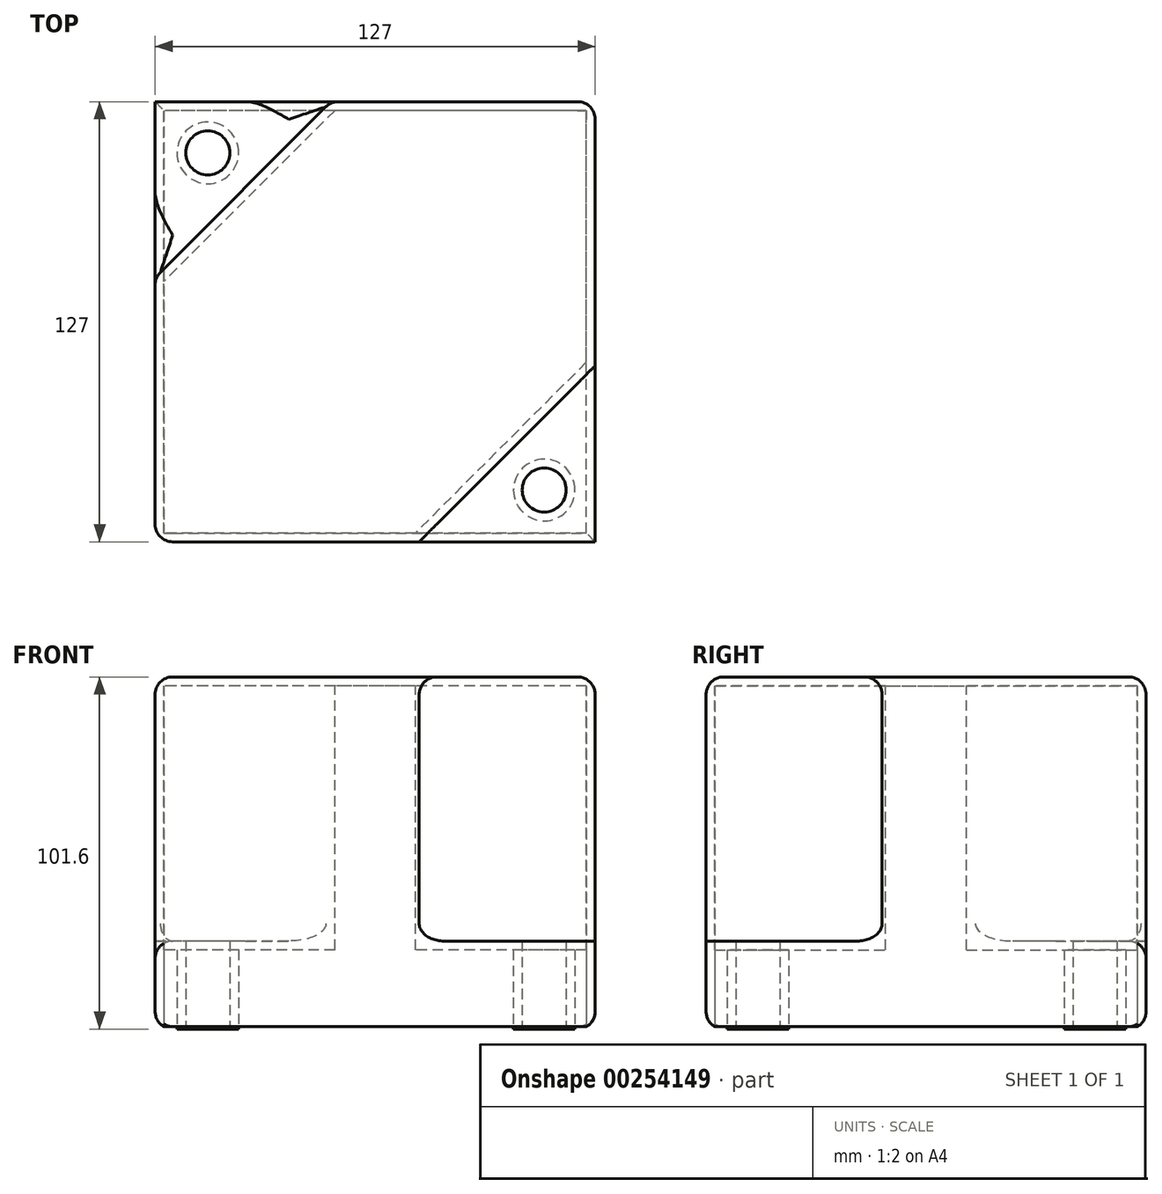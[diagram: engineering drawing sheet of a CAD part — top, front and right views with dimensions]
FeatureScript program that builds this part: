
annotation { "Feature Type Name" : "Feature", "Feature Type Description" : "" }
export const myFeature = defineFeature(function(context is Context, id is Id, definition is map)
    precondition{}
    {
        {
            var Q0;
            Q0=qCreatedBy(makeId("Top.planeOp"),FACE);
            var sketch = newSketch(context, id + "F0", { "sketchPlane" : qUnion([Q0])});
            skLineSegment(sketch, "E0.bottom", {"start": v(63.5, -63.5) * mm, "end": v(-63.5, -63.5) * mm});
            skLineSegment(sketch, "E0.top", {"start": v(63.5, 63.5) * mm, "end": v(-63.5, 63.5) * mm});
            skLineSegment(sketch, "E0.left", {"start": v(63.5, -63.5) * mm, "end": v(63.5, 63.5) * mm});
            skLineSegment(sketch, "E0.right", {"start": v(-63.5, -63.5) * mm, "end": v(-63.5, 63.5) * mm});
            skPoint(sketch, "E0.middle", {"position": v(0, 0) * mm});
            skSolve(sketch);
        }
        {
            var Q0;
            Q0=makeQuery(id+"F0.imprint","IMPRINT",FACE,{"disambiguationData":[TD([[makeQuery(id+"F0.imprint","IMPRINT",EDGE,{"derivedFrom":sQuery(id+"F0.wireOp",EDGE,"E0.bottom")}),-1.0]])]});
            extrude(context, id + "F1", {"entities" : qUnion([Q0]), "depth" : 101.6 * mm});
        }
        {
            var Q0;
            Q0=makeQuery(id+"F1.opExtrude","CAP_FACE",FACE,{"disambiguationData":[OSD([sQuery(id+"F0.wireOp",EDGE,"E0.bottom"),sQuery(id+"F0.wireOp",EDGE,"E0.top"),sQuery(id+"F0.wireOp",EDGE,"E0.left"),sQuery(id+"F0.wireOp",EDGE,"E0.right")])],"isStart":false});
            var sketch = newSketch(context, id + "F2", { "sketchPlane" : qUnion([Q0])});
            skLineSegment(sketch, "E1", {"start": v(-12.7, 63.5) * mm, "end": v(-63.5, 12.7) * mm});
            skLineSegment(sketch, "E2", {"start": v(63.5, -12.7) * mm, "end": v(12.7, -63.5) * mm});
            skSolve(sketch);
        }
        {
            var Q0;
            {var subQ0=sQuery(id+"F2.wireOp",EDGE,"E1");Q0=makeQuery(id+"F2.imprint","IMPRINT",FACE,{"disambiguationData":[TD([[makeQuery(id+"F2.imprint","IMPRINT",EDGE,{"derivedFrom":subQ0}),-1.0]])]});}
            var Q1;
            {var subQ0=sQuery(id+"F2.wireOp",EDGE,"E2");Q1=makeQuery(id+"F2.imprint","IMPRINT",FACE,{"disambiguationData":[TD([[makeQuery(id+"F2.imprint","IMPRINT",EDGE,{"derivedFrom":subQ0}),1.0]])]});}
            extrude(context, id + "F3", {"entities" : qUnion([Q0, Q1]), "operationType" : NewBodyOperationType.REMOVE, "oppositeDirection" : true, "depth" : 76.2 * mm});
        }
        {
            var Q0;
            Q0=qCreatedBy(makeId("Top.planeOp"),FACE);
            var sketch = newSketch(context, id + "F4", { "sketchPlane" : qUnion([Q0])});
            skCircle(sketch, "E3", {"center": v(48.8, -48.57) * mm, "radius": 6.35 * mm});
            skLineSegment(sketch, "E4", {"start": v(48.8, -48.57) * mm, "end": v(64.03, -48.57) * mm});
            skLineSegment(sketch, "E5", {"start": v(48.8, -48.57) * mm, "end": v(48.8, -63.81) * mm});
            skLineSegment(sketch, "E6", {"start": v(-63.54, 63.95) * mm, "end": v(-48.3, 63.95) * mm});
            skLineSegment(sketch, "E7", {"start": v(-63.54, 63.95) * mm, "end": v(-63.54, 48.71) * mm});
            skLineSegment(sketch, "E8", {"start": v(-48.3, 63.95) * mm, "end": v(-48.3, 48.71) * mm});
            skCircle(sketch, "E9", {"center": v(-48.3, 48.71) * mm, "radius": 6.35 * mm});
            skSolve(sketch);
        }
        {
            var Q0;
            Q0=makeQuery(id+"F4.imprint","IMPRINT",FACE,{"disambiguationData":[TD([[makeQuery(id+"F4.imprint","IMPRINT",EDGE,{"derivedFrom":sQuery(id+"F4.wireOp",EDGE,"E9")}),1.0]])]});
            var Q1;
            {var subQ0=sQuery(id+"F4.wireOp",EDGE,"E4");var subQ1=sQuery(id+"F4.wireOp",EDGE,"E3");var subQ2=makeQuery(id+"F4.imprint","INTERSECT",VERTEX,{"derivedFrom":[subQ1,subQ0]});Q1=makeQuery(id+"F4.imprint","IMPRINT",FACE,{"disambiguationData":[TD([[makeQuery(id+"F4.imprint","IMPRINT",EDGE,{"disambiguationData":[TD([[subQ2,-1.0]])],"derivedFrom":subQ1}),1.0]])]});}
            var Q2;
            {var subQ0=sQuery(id+"F4.wireOp",EDGE,"E4");var subQ1=sQuery(id+"F4.wireOp",EDGE,"E3");var subQ2=makeQuery(id+"F4.imprint","INTERSECT",VERTEX,{"derivedFrom":[subQ1,subQ0]});Q2=makeQuery(id+"F4.imprint","IMPRINT",FACE,{"disambiguationData":[TD([[makeQuery(id+"F4.imprint","IMPRINT",EDGE,{"disambiguationData":[TD([[subQ2,1.0]])],"derivedFrom":subQ1}),1.0]])]});}
            var Q3;
            Q3=makeQuery(id+"F3.boolean.opBoolean","COPY",FACE,{"derivedFrom":makeQuery(id+"F3.opExtrude","CAP_FACE",FACE,{"disambiguationData":[OSD([sQuery(id+"F0.wireOp",EDGE,"E0.bottom"),sQuery(id+"F0.wireOp",EDGE,"E0.left"),sQuery(id+"F2.wireOp",EDGE,"E2")])],"isStart":false})});
            extrude(context, id + "F5", {"entities" : qUnion([Q0, Q1, Q2]), "operationType" : NewBodyOperationType.REMOVE, "endBound" : BoundingType.UP_TO_SURFACE, "endBoundEntityFace" : qUnion([Q3]), "depth" : 203.2 * mm});
        }
        {
            var Q0;
            Q0=makeQuery(id+"F1.opExtrude","CAP_FACE",FACE,{"disambiguationData":[OSD([sQuery(id+"F0.wireOp",EDGE,"E0.bottom"),sQuery(id+"F0.wireOp",EDGE,"E0.top"),sQuery(id+"F0.wireOp",EDGE,"E0.left"),sQuery(id+"F0.wireOp",EDGE,"E0.right")])],"isStart":true});
            shell(context, id + "F6", {"entities" : qUnion([Q0]), "thickness" : 2.54 * mm});
        }
        {
            var Q0;
            Q0=makeQuery(id+"F3.boolean.opBoolean","COPY",EDGE,{"derivedFrom":makeQuery(id+"F3.opExtrude","CAP_EDGE",EDGE,{"disambiguationData":[OSD([sQuery(id+"F2.wireOp",EDGE,"E2")])],"isStart":true})});
            var Q1;
            Q1=makeQuery(id+"F1.opExtrude","CAP_EDGE",EDGE,{"disambiguationData":[OSD([sQuery(id+"F0.wireOp",EDGE,"E0.bottom")])],"isStart":false});
            var Q2;
            Q2=makeQuery(id+"F1.opExtrude","CAP_EDGE",EDGE,{"disambiguationData":[OSD([sQuery(id+"F0.wireOp",EDGE,"E0.left")])],"isStart":false});
            var Q3;
            Q3=makeQuery(id+"F1.opExtrude","CAP_EDGE",EDGE,{"disambiguationData":[OSD([sQuery(id+"F0.wireOp",EDGE,"E0.right")])],"isStart":false});
            var Q4;
            Q4=makeQuery(id+"F3.boolean.opBoolean","COPY",EDGE,{"derivedFrom":makeQuery(id+"F3.opExtrude","CAP_EDGE",EDGE,{"disambiguationData":[OSD([sQuery(id+"F2.wireOp",EDGE,"E1")])],"isStart":true})});
            var Q5;
            Q5=makeQuery(id+"F1.opExtrude","CAP_EDGE",EDGE,{"disambiguationData":[OSD([sQuery(id+"F0.wireOp",EDGE,"E0.top")])],"isStart":false});
            var Q6;
            Q6=makeQuery(id+"F3.boolean.opBoolean","COPY",EDGE,{"derivedFrom":makeQuery(id+"F3.opExtrude","CAP_EDGE",EDGE,{"disambiguationData":[OSD([sQuery(id+"F0.wireOp",EDGE,"E0.top")])],"isStart":false})});
            var Q7;
            Q7=makeQuery(id+"F3.boolean.opBoolean","COPY",EDGE,{"derivedFrom":makeQuery(id+"F3.opExtrude","SWEPT_EDGE",EDGE,{"disambiguationData":[OSD([sQuery(id+"F0.wireOp",EDGE,"E0.top"),sQuery(id+"F2.wireOp",EDGE,"E1")])]})});
            var Q8;
            Q8=makeQuery(id+"F3.boolean.opBoolean","COPY",FACE,{"derivedFrom":makeQuery(id+"F3.opExtrude","SWEPT_FACE",FACE,{"disambiguationData":[OSD([sQuery(id+"F2.wireOp",EDGE,"E1")])]})});
            var Q9;
            Q9=makeQuery(id+"F3.boolean.opBoolean","COPY",EDGE,{"derivedFrom":makeQuery(id+"F3.opExtrude","SWEPT_EDGE",EDGE,{"disambiguationData":[OSD([sQuery(id+"F0.wireOp",EDGE,"E0.bottom"),sQuery(id+"F2.wireOp",EDGE,"E2")])]})});
            var Q10;
            Q10=makeQuery(id+"F3.boolean.opBoolean","COPY",EDGE,{"derivedFrom":makeQuery(id+"F3.opExtrude","SWEPT_EDGE",EDGE,{"disambiguationData":[OSD([sQuery(id+"F0.wireOp",EDGE,"E0.left"),sQuery(id+"F2.wireOp",EDGE,"E2")])]})});
            var Q11;
            Q11=makeQuery(id+"F3.boolean.opBoolean","COPY",EDGE,{"derivedFrom":makeQuery(id+"F3.opExtrude","CAP_EDGE",EDGE,{"disambiguationData":[OSD([sQuery(id+"F0.wireOp",EDGE,"E0.left")])],"isStart":false})});
            var Q12;
            Q12=makeQuery(id+"F3.boolean.opBoolean","COPY",EDGE,{"derivedFrom":makeQuery(id+"F3.opExtrude","CAP_EDGE",EDGE,{"disambiguationData":[OSD([sQuery(id+"F0.wireOp",EDGE,"E0.bottom")])],"isStart":false})});
            var Q13;
            Q13=makeQuery(id+"F1.opExtrude","CAP_EDGE",EDGE,{"disambiguationData":[OSD([sQuery(id+"F0.wireOp",EDGE,"E0.left")])],"isStart":true});
            var Q14;
            Q14=makeQuery(id+"F1.opExtrude","CAP_EDGE",EDGE,{"disambiguationData":[OSD([sQuery(id+"F0.wireOp",EDGE,"E0.bottom")])],"isStart":true});
            fillet(context, id + "F7", {"entities" : qUnion([Q0, Q1, Q2, Q3, Q4, Q5, Q6, Q7, Q8, Q9, Q10, Q11, Q12, Q13, Q14]), "radius" : 5.08 * mm, "tangentPropagation" : true, "allowEdgeOverflow" : false});
        }
        {
            var Q0;
            Q0=makeQuery(id+"F1.opExtrude","SWEPT_EDGE",EDGE,{"disambiguationData":[OSD([sQuery(id+"F0.wireOp",EDGE,"E0.bottom"),sQuery(id+"F0.wireOp",EDGE,"E0.right")])]});
            var Q1;
            Q1=makeQuery(id+"F1.opExtrude","SWEPT_EDGE",EDGE,{"disambiguationData":[OSD([sQuery(id+"F0.wireOp",EDGE,"E0.top"),sQuery(id+"F0.wireOp",EDGE,"E0.left")])]});
            var Q2;
            Q2=makeQuery(id+"F3.boolean.opBoolean","COPY",EDGE,{"derivedFrom":makeQuery(id+"F3.opExtrude","CAP_EDGE",EDGE,{"disambiguationData":[OSD([sQuery(id+"F2.wireOp",EDGE,"E2")])],"isStart":false})});
            fillet(context, id + "F8", {"entities" : qUnion([Q0, Q1, Q2]), "radius" : 5.08 * mm, "tangentPropagation" : true, "allowEdgeOverflow" : false});
        }
    });
